# Revit family: RN 31161 Interbloc
name_source: partatom
category: Rohrzubehör
units: mm (PartAtom-declared; Revit-internal decimal feet)

## family parameters
Arbeitsebenenbasiert = Nein
Beim Laden mit Abzugskörper schneiden = Nein
Bemaßung runder Anschluss = Durchmesser verwenden
Gemeinsam genutzt = Nein
Immer vertikal = Ja
Teiletyp = Ventil - Zerlegung in

## types (2) — shared parameters
1.010.00.2 Blattnummer der Richtlinie = 17
1.010.00.3 Ausgabedatum (Monat) der Richtlinie = 201601
1.010.00.4 Herstellername = R. Nussbaum AG
1.010.00.5 Revisionsdatum der Datei = 20190528
1.010.00.6 Webadresse des Herstellers = http://www.nussbaum.ch
1.100.00.3 Sortiernummer für Anzeigereihenfolge = 5
1.100.00.4 Produktbezeichnung = Sicherheitsarmaturen
1.960/3L.00.8 Link (URL) = https://www.nussbaum.ch
17.700.00.4 Armaturentyp = 6
17.700.00.6 kvs-Wert [m3/h] = 21.25
17.700.00.7 Maximale Betriebstemperatur TB [°C] = 90
17.700.00.8 Maximaler Betriebsdruck (Arbeitsdruck) ps [1.0 · 105 Pa] = 10
CONNECTOR0_ref_dZ = 6 mm  [stored 0.019685 ft]
CONNECTOR1_dZ_00 = 42 mm
CONNECTOR1_dZ_01 = 54 mm
CONNECTOR1_ref_dX = 79 mm
CONNECTOR1_ref_dZ = 54 mm
CONNECTOR2_dZ_00 = 42 mm
CONNECTOR2_dZ_01 = 54 mm
CONNECTOR2_ref_dX = 81 mm
CONNECTOR2_ref_dZ = 54 mm
CONNECTOR3_DIAMETER_dZ_0r = 20 mm
CONNECTOR3_dZ_00 = 36 mm
CONNECTOR3_dZ_01 = 21 mm
CONNECTOR3_ref_dX = 156 mm
CONNECTOR3_ref_dZ = 21 mm
Connector Visibility = Nein
EnclosingSpace Visibility = Nein
Hersteller = R. Nussbauzm AG
URL = https://www.nussbaum.ch

## per-type parameters (varying)
| type | 1.800.00.3 TGA-Nummer | 1.810.00.3 Hersteller-Bestellnummer | 1.810.00.4 DATANORM-Nummer | 1.810.00.6 GTIN-Nummer | 17.700.00.30 Produktbeschreibung | 17.700.00.5 Nennweite DN | CONNECTOR0_DIAMETER_dX_0r | CONNECTOR0_dX_00 | CONNECTOR0_dX_01 | CONNECTOR0_ref_dX | CONNECTOR1_DIAMETER_dZ_0r | CONNECTOR2_DIAMETER_dZ_0r | Modell | R. Nussbaum AG 31161.36 de Visibility | R. Nussbaum AG 31161.37 de Visibility | Typenkommentare |
| DN 25 | 00501600000000000000000000000200700000000000000001???00000 | 31161.36 | 31161.36 | 7612945738141 | 31161.36, Interbloc, ohne Anschlussverschraubungen, DN=25, R=½, Rp=1 | 25 | 20 mm | 136 mm | 121 mm | 121 mm | 20 mm | 20 mm | 31161.36 | Ja | Nein | InterblocDN 25 |
| DN 32 | 00501600000000000000000000000200700000000000000002???00000 | 31161.37 | 31161.37 | 7612945738158 | 31161.37, Interbloc, ohne Anschlussverschraubungen, DN=32, R=½, Rp=1¼ | 32 | 32 mm | 143 mm | 124 mm | 124 mm | 25 mm  [stored 0.082021 ft] | 25 mm  [stored 0.082021 ft] | 31161.37 | Nein | Ja | InterblocDN 32 |

note: [stored X ft] marks values corroborated as IEEE doubles in the binary element streams (Revit-internal decimal feet)
